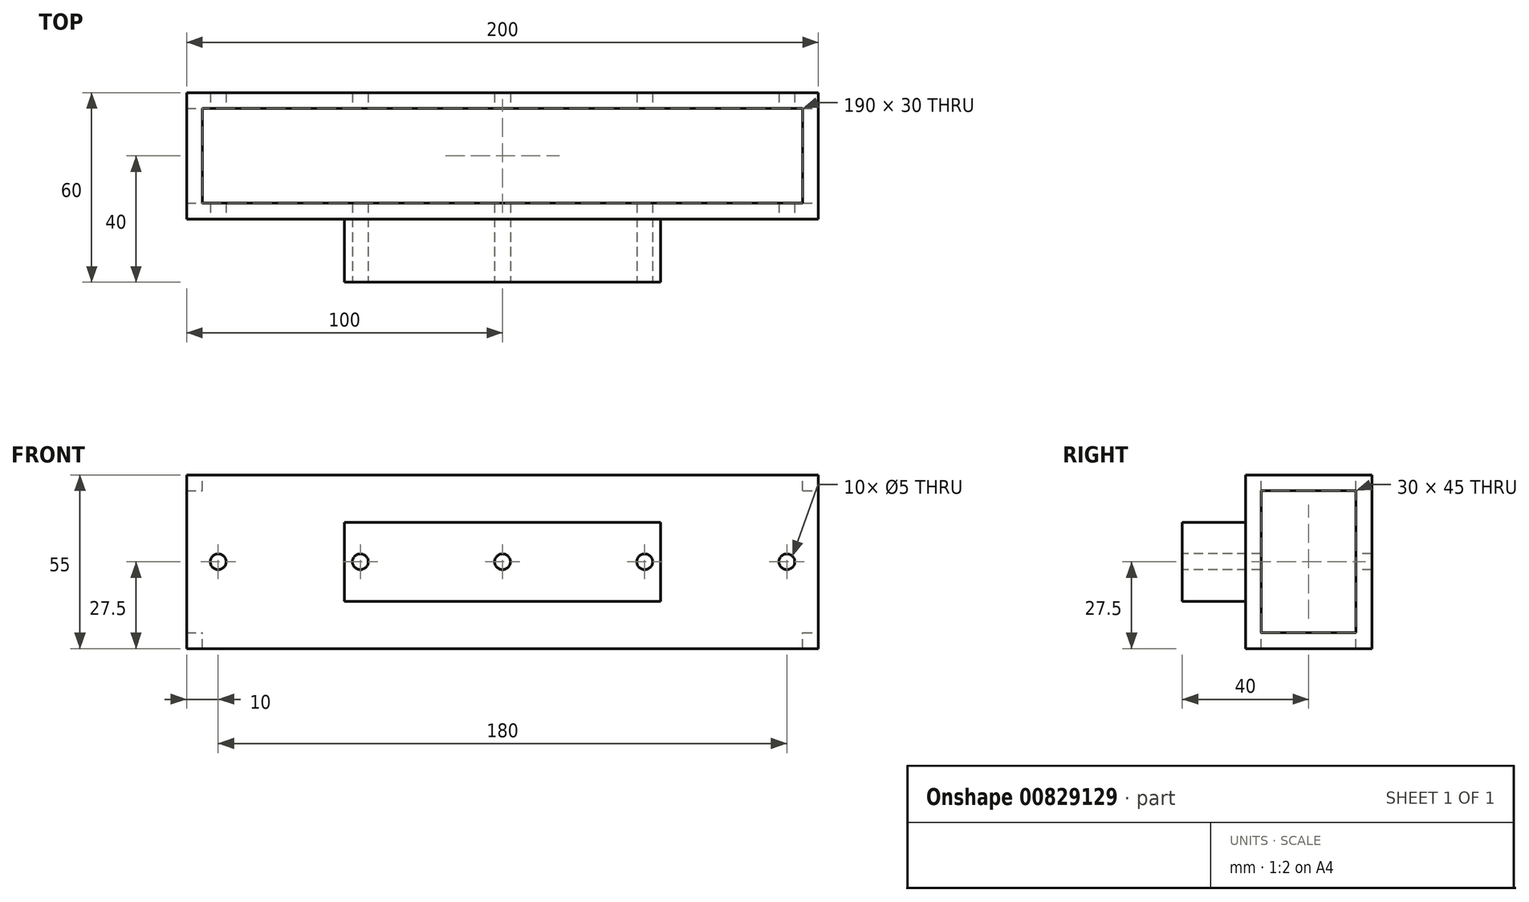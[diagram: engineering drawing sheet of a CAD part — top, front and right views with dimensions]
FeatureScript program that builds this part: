
annotation { "Feature Type Name" : "Feature", "Feature Type Description" : "" }
export const myFeature = defineFeature(function(context is Context, id is Id, definition is map)
    precondition{}
    {
        {
            var Q0;
            Q0=qCreatedBy(makeId("Top.planeOp"),FACE);
            var sketch = newSketch(context, id + "F0", { "sketchPlane" : qUnion([Q0])});
            skLineSegment(sketch, "E0.bottom", {"start": v(-100, 0) * mm, "end": v(100, 0) * mm});
            skLineSegment(sketch, "E0.top", {"start": v(-100, -40) * mm, "end": v(100, -40) * mm});
            skLineSegment(sketch, "E0.left", {"start": v(-100, 0) * mm, "end": v(-100, -40) * mm});
            skLineSegment(sketch, "E0.right", {"start": v(100, 0) * mm, "end": v(100, -40) * mm});
            skLineSegment(sketch, "E1.bottom", {"start": v(-50, -40) * mm, "end": v(50, -40) * mm});
            skLineSegment(sketch, "E1.top", {"start": v(-50, -60) * mm, "end": v(50, -60) * mm});
            skLineSegment(sketch, "E1.left", {"start": v(-50, -40) * mm, "end": v(-50, -60) * mm});
            skLineSegment(sketch, "E1.right", {"start": v(50, -40) * mm, "end": v(50, -60) * mm});
            skSolve(sketch);
        }
        {
            var Q0;
            Q0=makeQuery(id+"F0.imprint","IMPRINT",FACE,{"disambiguationData":[TD([[makeQuery(id+"F0.imprint","IMPRINT",EDGE,{"derivedFrom":sQuery(id+"F0.wireOp",EDGE,"E0.bottom")}),-1.0]])]});
            var Q1;
            Q1=makeQuery(id+"F0.imprint","IMPRINT",FACE,{"disambiguationData":[TD([[makeQuery(id+"F0.imprint","IMPRINT",EDGE,{"derivedFrom":sQuery(id+"F0.wireOp",EDGE,"E1.top")}),1.0]])]});
            extrude(context, id + "F1", {"entities" : qUnion([Q0, Q1]), "endBound" : BoundingType.SYMMETRIC, "depth" : 55 * mm, "offsetDistance" : 25 * mm});
        }
        {
            var Q0;
            Q0=makeQuery(id+"F1.opExtrude","CAP_FACE",FACE,{"disambiguationData":[OSD([sQuery(id+"F0.wireOp",EDGE,"E0.bottom"),sQuery(id+"F0.wireOp",EDGE,"E0.top"),sQuery(id+"F0.wireOp",EDGE,"E0.left"),sQuery(id+"F0.wireOp",EDGE,"E0.right"),sQuery(id+"F0.wireOp",EDGE,"E1.top"),sQuery(id+"F0.wireOp",EDGE,"E1.left"),sQuery(id+"F0.wireOp",EDGE,"E1.right")])],"isStart":false});
            var sketch = newSketch(context, id + "F2", { "sketchPlane" : qUnion([Q0])});
            skLineSegment(sketch, "E2.bottom", {"start": v(95, -5) * mm, "end": v(-95, -5) * mm});
            skLineSegment(sketch, "E2.top", {"start": v(95, -35) * mm, "end": v(-95, -35) * mm});
            skLineSegment(sketch, "E2.left", {"start": v(95, -5) * mm, "end": v(95, -35) * mm});
            skLineSegment(sketch, "E2.right", {"start": v(-95, -5) * mm, "end": v(-95, -35) * mm});
            skPoint(sketch, "E2.middle", {"position": v(0, -20) * mm});
            skSolve(sketch);
        }
        {
            var Q0;
            Q0=makeQuery(id+"F2.imprint","IMPRINT",FACE,{"disambiguationData":[TD([[makeQuery(id+"F2.imprint","IMPRINT",EDGE,{"derivedFrom":sQuery(id+"F2.wireOp",EDGE,"E2.bottom")}),1.0]])]});
            extrude(context, id + "F3", {"entities" : qUnion([Q0]), "operationType" : NewBodyOperationType.REMOVE, "endBound" : BoundingType.THROUGH_ALL, "oppositeDirection" : true, "depth" : 25 * mm, "offsetDistance" : 25 * mm});
        }
        {
            var Q0;
            Q0=makeQuery(id+"F3.boolean.opBoolean","COPY",FACE,{"derivedFrom":makeQuery(id+"F3.opExtrude","SWEPT_FACE",FACE,{"disambiguationData":[OSD([sQuery(id+"F2.wireOp",EDGE,"E2.right")])]})});
            var sketch = newSketch(context, id + "F4", { "sketchPlane" : qUnion([Q0])});
            skLineSegment(sketch, "E3.bottom", {"start": v(-35, 22.5) * mm, "end": v(-5, 22.5) * mm});
            skLineSegment(sketch, "E3.top", {"start": v(-35, -22.5) * mm, "end": v(-5, -22.5) * mm});
            skLineSegment(sketch, "E3.left", {"start": v(-35, 22.5) * mm, "end": v(-35, -22.5) * mm});
            skLineSegment(sketch, "E3.right", {"start": v(-5, 22.5) * mm, "end": v(-5, -22.5) * mm});
            skPoint(sketch, "E3.middle", {"position": v(-20, 0) * mm});
            skSolve(sketch);
        }
        {
            var Q0;
            Q0 = qSketchRegion(id + "F4", true);
            extrude(context, id + "F5", {"entities" : qUnion([Q0]), "operationType" : NewBodyOperationType.REMOVE, "endBound" : BoundingType.SYMMETRIC, "oppositeDirection" : true, "depth" : 1000 * mm, "offsetDistance" : 25 * mm});
        }
        {
            var Q0;
            {var subQ0=sQuery(id+"F0.wireOp",EDGE,"E0.top");Q0=makeQuery(id+"F1.opExtrude","SWEPT_FACE",FACE,{"disambiguationData":[OSD([subQ0]),TDD([makeQuery(id+"F0.imprint","IMPRINT",EDGE,{"disambiguationData":[TD([[makeQuery(id+"F0.imprint","INTERSECT",VERTEX,{"derivedFrom":[subQ0,sQuery(id+"F0.wireOp",EDGE,"E1.left")]}),1.0]])],"derivedFrom":subQ0})])]});}
            var sketch = newSketch(context, id + "F6", { "sketchPlane" : qUnion([Q0])});
            skCircle(sketch, "E4", {"center": v(-90, 0) * mm, "radius": 2.5 * mm});
            skCircle(sketch, "E5", {"center": v(90, 0) * mm, "radius": 2.5 * mm});
            skSolve(sketch);
        }
        {
            var Q0;
            Q0=makeQuery(id+"F6.imprint","IMPRINT",FACE,{"disambiguationData":[TD([[makeQuery(id+"F6.imprint","IMPRINT",EDGE,{"derivedFrom":sQuery(id+"F6.wireOp",EDGE,"E4")}),1.0]])]});
            var Q1;
            Q1=makeQuery(id+"F6.imprint","IMPRINT",FACE,{"disambiguationData":[TD([[makeQuery(id+"F6.imprint","IMPRINT",EDGE,{"derivedFrom":sQuery(id+"F6.wireOp",EDGE,"E5")}),1.0]])]});
            extrude(context, id + "F7", {"entities" : qUnion([Q0, Q1]), "operationType" : NewBodyOperationType.REMOVE, "endBound" : BoundingType.THROUGH_ALL, "oppositeDirection" : true, "depth" : 10 * mm, "offsetDistance" : 25 * mm});
        }
        {
            var Q0;
            Q0=makeQuery(id+"F1.opExtrude","SWEPT_FACE",FACE,{"disambiguationData":[OSD([sQuery(id+"F0.wireOp",EDGE,"E1.top")])]});
            var sketch = newSketch(context, id + "F8", { "sketchPlane" : qUnion([Q0])});
            skCircle(sketch, "E6", {"center": v(-45, 0) * mm, "radius": 2.5 * mm});
            skCircle(sketch, "E7", {"center": v(45, 0) * mm, "radius": 2.5 * mm});
            skSolve(sketch);
        }
        {
            var Q0;
            Q0 = qSketchRegion(id + "F8", true);
            extrude(context, id + "F9", {"entities" : qUnion([Q0]), "operationType" : NewBodyOperationType.REMOVE, "endBound" : BoundingType.THROUGH_ALL, "oppositeDirection" : true, "depth" : 25 * mm, "offsetDistance" : 25 * mm});
        }
        {
            var Q0;
            Q0=makeQuery(id+"F1.opExtrude","SWEPT_FACE",FACE,{"disambiguationData":[OSD([sQuery(id+"F0.wireOp",EDGE,"E1.top")])]});
            var sketch = newSketch(context, id + "F10", { "sketchPlane" : qUnion([Q0])});
            skCircle(sketch, "E8", {"center": v(0, 0) * mm, "radius": 2.5 * mm});
            skSolve(sketch);
        }
        {
            var Q0;
            Q0 = qSketchRegion(id + "F10", true);
            extrude(context, id + "F11", {"entities" : qUnion([Q0]), "operationType" : NewBodyOperationType.REMOVE, "endBound" : BoundingType.THROUGH_ALL, "oppositeDirection" : true, "depth" : 25 * mm, "offsetDistance" : 25 * mm});
        }
        {
            var Q0;
            Q0=makeQuery(id+"F1.opExtrude","SWEPT_FACE",FACE,{"disambiguationData":[OSD([sQuery(id+"F0.wireOp",EDGE,"E1.top")])]});
            var sketch = newSketch(context, id + "F12", { "sketchPlane" : qUnion([Q0])});
            skLineSegment(sketch, "E9.bottom", {"start": v(50, 12.5) * mm, "end": v(-50, 12.5) * mm});
            skLineSegment(sketch, "E9.top", {"start": v(50, -12.5) * mm, "end": v(-50, -12.5) * mm});
            skLineSegment(sketch, "E9.left", {"start": v(50, 12.5) * mm, "end": v(50, -12.5) * mm});
            skLineSegment(sketch, "E9.right", {"start": v(-50, 12.5) * mm, "end": v(-50, -12.5) * mm});
            skPoint(sketch, "E9.middle", {"position": v(0, 0) * mm});
            skLineSegment(sketch, "E10.bottom", {"start": v(73, 42.32) * mm, "end": v(-73, 42.32) * mm});
            skLineSegment(sketch, "E10.top", {"start": v(73, -42.32) * mm, "end": v(-73, -42.32) * mm});
            skLineSegment(sketch, "E10.left", {"start": v(73, 42.32) * mm, "end": v(73, -42.32) * mm});
            skLineSegment(sketch, "E10.right", {"start": v(-73, 42.32) * mm, "end": v(-73, -42.32) * mm});
            skSolve(sketch);
        }
        {
            var Q0;
            Q0 = qSketchRegion(id + "F12", true);
            var Q1;
            {var subQ0=sQuery(id+"F0.wireOp",EDGE,"E0.top");Q1=makeQuery(id+"F1.opExtrude","SWEPT_FACE",FACE,{"disambiguationData":[OSD([subQ0]),TDD([makeQuery(id+"F0.imprint","IMPRINT",EDGE,{"disambiguationData":[TD([[makeQuery(id+"F0.imprint","INTERSECT",VERTEX,{"derivedFrom":[subQ0,sQuery(id+"F0.wireOp",EDGE,"E0.right")]}),1.0]])],"derivedFrom":subQ0})])]});}
            extrude(context, id + "F13", {"entities" : qUnion([Q0]), "operationType" : NewBodyOperationType.REMOVE, "endBound" : BoundingType.UP_TO_SURFACE, "oppositeDirection" : true, "depth" : 25 * mm, "endBoundEntityFace" : qUnion([Q1]), "offsetDistance" : 25 * mm});
        }
    });
